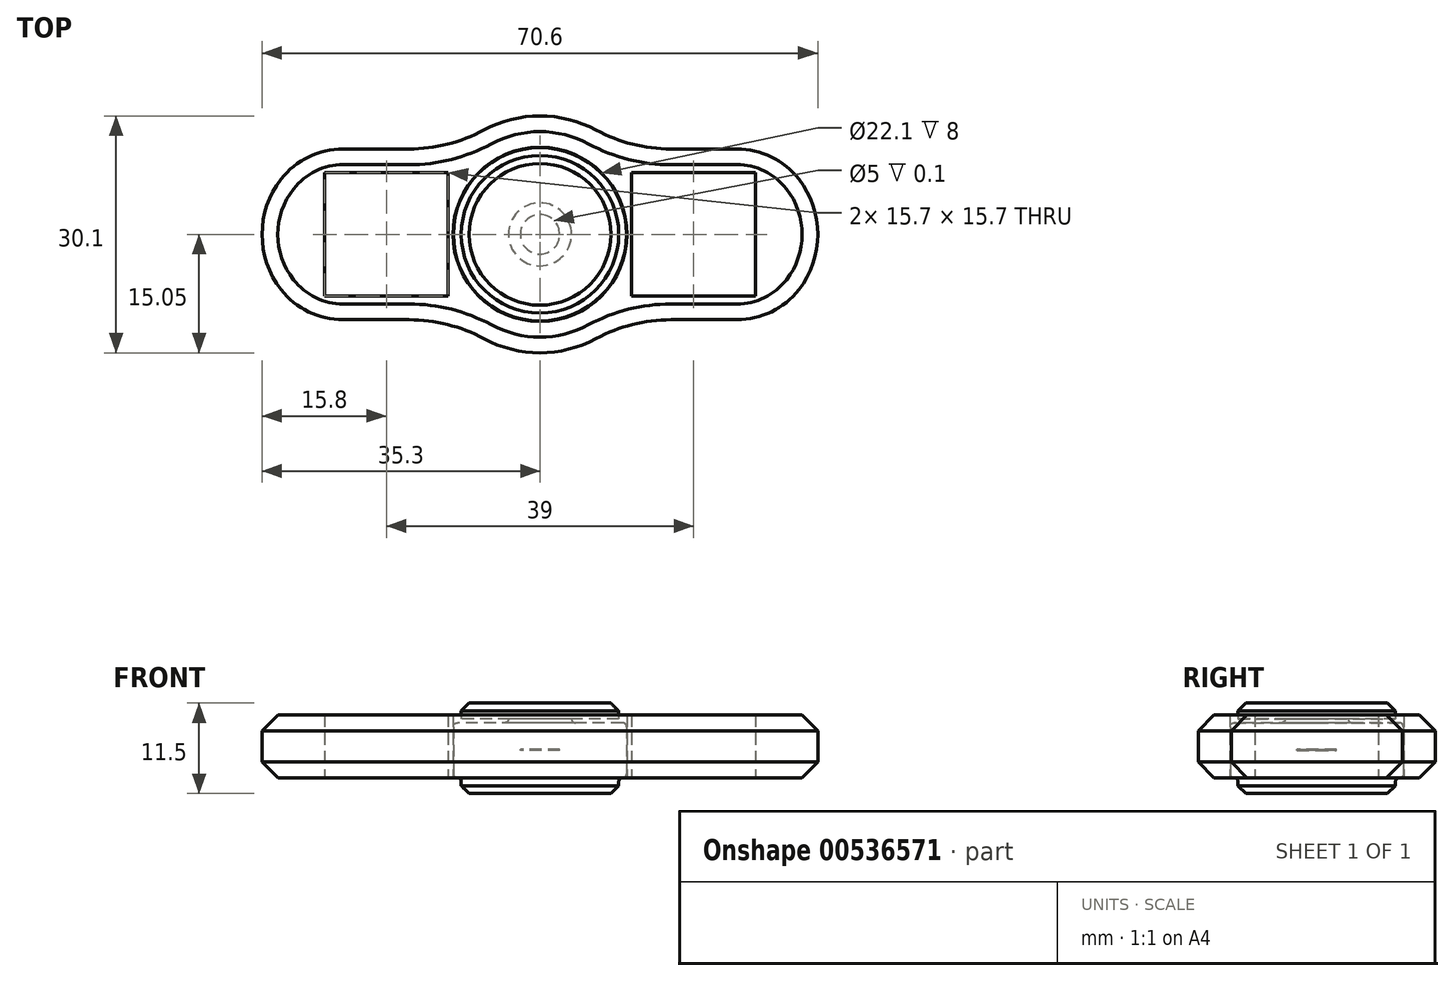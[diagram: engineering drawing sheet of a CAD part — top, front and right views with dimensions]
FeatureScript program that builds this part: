
annotation { "Feature Type Name" : "Feature", "Feature Type Description" : "" }
export const myFeature = defineFeature(function(context is Context, id is Id, definition is map)
    precondition{}
    {
        {
            var Q0;
            Q0=qCreatedBy(makeId("Top.planeOp"),FACE);
            var sketch = newSketch(context, id + "F0", { "sketchPlane" : qUnion([Q0])});
            skCircle(sketch, "E0", {"center": v(0, 0) * mm, "radius": 11 * mm});
            skCircle(sketch, "E1", {"center": v(0, 0) * mm, "radius": 4 * mm});
            skSolve(sketch);
        }
        {
            var Q0;
            Q0=makeQuery(id+"F0.imprint","IMPRINT",FACE,{"disambiguationData":[TD([[makeQuery(id+"F0.imprint","IMPRINT",EDGE,{"derivedFrom":sQuery(id+"F0.wireOp",EDGE,"E0")}),1.0]])]});
            extrude(context, id + "F1", {"entities" : qUnion([Q0]), "depth" : 7 * mm, "offsetDistance" : 25 * mm});
        }
        {
            var Q0;
            Q0=makeQuery(id+"F1.opExtrude","CAP_FACE",FACE,{"disambiguationData":[OSD([sQuery(id+"F0.wireOp",EDGE,"E0"),sQuery(id+"F0.wireOp",EDGE,"E1")])],"isStart":true});
            var sketch = newSketch(context, id + "F2", { "sketchPlane" : qUnion([Q0])});
            skCircle(sketch, "E2.0", {"center": v(0, 0) * mm, "radius": 11.05 * mm});
            skCircle(sketch, "E3.0", {"center": v(0, 0) * mm, "radius": 15.05 * mm});
            skLineSegment(sketch, "E4", {"start": v(0, 0) * mm, "end": v(-19.5, 0) * mm, "construction": true});
            skLineSegment(sketch, "E5.bottom", {"start": v(-27.35, -7.85) * mm, "end": v(-11.65, -7.85) * mm});
            skLineSegment(sketch, "E5.top", {"start": v(-27.35, 7.85) * mm, "end": v(-11.65, 7.85) * mm});
            skLineSegment(sketch, "E5.left", {"start": v(-27.35, -7.85) * mm, "end": v(-27.35, 7.85) * mm});
            skLineSegment(sketch, "E5.right", {"start": v(-11.65, -7.85) * mm, "end": v(-11.65, 7.85) * mm});
            skPoint(sketch, "E5.middle", {"position": v(-19.5, 0) * mm});
            skCircle(sketch, "E6", {"center": v(0, 0) * mm, "radius": 50 * mm, "construction": true});
            skLineSegment(sketch, "E7", {"start": v(-19.5, 0) * mm, "end": v(-35.3, 0) * mm, "construction": true});
            skLineSegment(sketch, "E8", {"start": v(-27.35, 7.85) * mm, "end": v(-27.35, 10.85) * mm, "construction": true});
            skLineSegment(sketch, "E9.0", {"start": v(-23, 10.85) * mm, "end": v(-27.35, 10.85) * mm});
            skLineSegment(sketch, "E9.1", {"start": v(0, 10.85) * mm, "end": v(-2.1, 10.85) * mm, "construction": true});
            skLineSegment(sketch, "E10.trimOffspring", {"start": v(-10.43, 10.85) * mm, "end": v(-23, 10.85) * mm});
            skLineSegment(sketch, "E11.MirrorCS", {"start": v(-10.43, -10.85) * mm, "end": v(-23, -10.85) * mm});
            skLineSegment(sketch, "E12.MirrorCS", {"start": v(-23, -10.85) * mm, "end": v(-27.35, -10.85) * mm});
            skArc(sketch, "E13", {"start": v(-27.35, 10.85) * mm, "mid": v(-35.3, 0) * mm, "end": v(-27.35, -10.85) * mm});
            skLineSegment(sketch, "E14.1.0", {"start": v(27.35, 7.85) * mm, "end": v(11.65, 7.85) * mm});
            skLineSegment(sketch, "E14.1.1", {"start": v(11.65, 7.85) * mm, "end": v(11.65, -7.85) * mm});
            skLineSegment(sketch, "E14.1.2", {"start": v(27.35, -7.85) * mm, "end": v(11.65, -7.85) * mm});
            skLineSegment(sketch, "E14.1.3", {"start": v(10.43, -10.85) * mm, "end": v(23, -10.85) * mm});
            skLineSegment(sketch, "E14.1.4", {"start": v(23, -10.85) * mm, "end": v(27.35, -10.85) * mm});
            skLineSegment(sketch, "E14.1.5", {"start": v(27.35, 7.85) * mm, "end": v(27.35, -7.85) * mm});
            skArc(sketch, "E14.1.6", {"start": v(27.35, -10.85) * mm, "mid": v(35.3, 0) * mm, "end": v(27.35, 10.85) * mm});
            skLineSegment(sketch, "E14.1.7", {"start": v(23, 10.85) * mm, "end": v(27.35, 10.85) * mm});
            skLineSegment(sketch, "E14.1.8", {"start": v(10.43, 10.85) * mm, "end": v(23, 10.85) * mm});
            skCircle(sketch, "E15", {"center": v(0, 0) * mm, "radius": 29.42 * mm, "construction": true});
            skSolve(sketch);
        }
        {
            var Q0;
            {var subQ5=sQuery(id+"F2.wireOp",EDGE,"E14.2.0");Q0=makeQuery(id+"F2.imprint","IMPRINT",FACE,{"disambiguationData":[TD([[makeQuery(id+"F2.imprint","IMPRINT",EDGE,{"derivedFrom":subQ5}),-1.0]])]});}
            var Q1;
            Q1=makeQuery(id+"F2.imprint","IMPRINT",FACE,{"disambiguationData":[TD([[makeQuery(id+"F2.imprint","IMPRINT",EDGE,{"derivedFrom":sQuery(id+"F2.wireOp",EDGE,"E2.0")}),-1.0]])]});
            var Q2;
            {var subQ6=sQuery(id+"F2.wireOp",EDGE,"E14.1.0");Q2=makeQuery(id+"F2.imprint","IMPRINT",FACE,{"disambiguationData":[TD([[makeQuery(id+"F2.imprint","IMPRINT",EDGE,{"derivedFrom":subQ6}),-1.0]])]});}
            var Q3;
            {var subQ5=sQuery(id+"F2.wireOp",EDGE,"E5.bottom");Q3=makeQuery(id+"F2.imprint","IMPRINT",FACE,{"disambiguationData":[TD([[makeQuery(id+"F2.imprint","IMPRINT",EDGE,{"derivedFrom":subQ5}),-1.0]])]});}
            extrude(context, id + "F3", {"entities" : qUnion([Q0, Q1, Q2, Q3]), "oppositeDirection" : true, "depth" : 8 * mm, "offsetDistance" : 25 * mm});
        }
        {
            var Q0;
            Q0=makeQuery(id+"F3.opExtrude","SWEPT_EDGE",EDGE,{"disambiguationData":[OSD([sQuery(id+"F2.wireOp",EDGE,"E3.0"),sQuery(id+"F2.wireOp",EDGE,"E14.2.3")])]});
            var Q1;
            Q1=makeQuery(id+"F3.opExtrude","SWEPT_EDGE",EDGE,{"disambiguationData":[OSD([sQuery(id+"F2.wireOp",EDGE,"E3.0"),sQuery(id+"F2.wireOp",EDGE,"E14.1.8")])]});
            var Q2;
            Q2=makeQuery(id+"F3.opExtrude","SWEPT_EDGE",EDGE,{"disambiguationData":[OSD([sQuery(id+"F2.wireOp",EDGE,"E3.0"),sQuery(id+"F2.wireOp",EDGE,"E14.2.8")])]});
            var Q3;
            Q3=makeQuery(id+"F3.opExtrude","SWEPT_EDGE",EDGE,{"disambiguationData":[OSD([sQuery(id+"F2.wireOp",EDGE,"E3.0"),sQuery(id+"F2.wireOp",EDGE,"E10.trimOffspring")])]});
            var Q4;
            Q4=makeQuery(id+"F3.opExtrude","SWEPT_EDGE",EDGE,{"disambiguationData":[OSD([sQuery(id+"F2.wireOp",EDGE,"E3.0"),sQuery(id+"F2.wireOp",EDGE,"E11.MirrorCS")])]});
            var Q5;
            Q5=makeQuery(id+"F3.opExtrude","SWEPT_EDGE",EDGE,{"disambiguationData":[OSD([sQuery(id+"F2.wireOp",EDGE,"E3.0"),sQuery(id+"F2.wireOp",EDGE,"E14.1.3")])]});
            fillet(context, id + "F4", {"entities" : qUnion([Q0, Q1, Q2, Q3, Q4, Q5]), "radius" : 20 * mm, "tangentPropagation" : true, "allowEdgeOverflow" : false});
        }
        {
            var Q0;
            Q0=makeQuery(id+"F3.opExtrude","SWEPT_EDGE",EDGE,{"disambiguationData":[OSD([sQuery(id+"F2.wireOp",EDGE,"E14.2.4"),sQuery(id+"F2.wireOp",EDGE,"E14.2.6")])]});
            var Q1;
            Q1=makeQuery(id+"F3.opExtrude","SWEPT_EDGE",EDGE,{"disambiguationData":[OSD([sQuery(id+"F2.wireOp",EDGE,"E14.2.6"),sQuery(id+"F2.wireOp",EDGE,"E14.2.7")])]});
            var Q2;
            Q2=makeQuery(id+"F3.opExtrude","SWEPT_EDGE",EDGE,{"disambiguationData":[OSD([sQuery(id+"F2.wireOp",EDGE,"E9.0"),sQuery(id+"F2.wireOp",EDGE,"E13")])]});
            var Q3;
            Q3=makeQuery(id+"F3.opExtrude","SWEPT_EDGE",EDGE,{"disambiguationData":[OSD([sQuery(id+"F2.wireOp",EDGE,"E12.MirrorCS"),sQuery(id+"F2.wireOp",EDGE,"E13")])]});
            var Q4;
            Q4=makeQuery(id+"F3.opExtrude","SWEPT_EDGE",EDGE,{"disambiguationData":[OSD([sQuery(id+"F2.wireOp",EDGE,"E14.1.4"),sQuery(id+"F2.wireOp",EDGE,"E14.1.6")])]});
            var Q5;
            Q5=makeQuery(id+"F3.opExtrude","SWEPT_EDGE",EDGE,{"disambiguationData":[OSD([sQuery(id+"F2.wireOp",EDGE,"E14.1.6"),sQuery(id+"F2.wireOp",EDGE,"E14.1.7")])]});
            fillet(context, id + "F5", {"entities" : qUnion([Q0, Q1, Q2, Q3, Q4, Q5]), "radius" : 10 * mm, "tangentPropagation" : true, "allowEdgeOverflow" : false});
        }
        {
            var Q0;
            Q0=makeQuery(id+"F3.opExtrude","CAP_EDGE",EDGE,{"disambiguationData":[OSD([sQuery(id+"F2.wireOp",EDGE,"E14.2.6")])],"isStart":false});
            var Q1;
            Q1=makeQuery(id+"F3.opExtrude","CAP_EDGE",EDGE,{"disambiguationData":[OSD([sQuery(id+"F2.wireOp",EDGE,"E14.1.6")])],"isStart":false});
            var Q2;
            {var subQ0=sQuery(id+"F2.wireOp",EDGE,"E13");var subQ1=sQuery(id+"F2.wireOp",EDGE,"E9.0");Q2=makeQuery(id+"F5.opFillet","BLEND_EDGE",EDGE,{"blendedFrom":[makeQuery(id+"F3.opExtrude","SWEPT_EDGE",EDGE,{"disambiguationData":[OSD([subQ1,subQ0])]}),makeQuery(id+"F3.opExtrude","CAP_FACE",FACE,{"disambiguationData":[OSD([sQuery(id+"F2.wireOp",EDGE,"E2.0"),sQuery(id+"F2.wireOp",EDGE,"E3.0"),sQuery(id+"F2.wireOp",EDGE,"E5.bottom"),sQuery(id+"F2.wireOp",EDGE,"E5.top"),sQuery(id+"F2.wireOp",EDGE,"E5.left"),sQuery(id+"F2.wireOp",EDGE,"E5.right"),subQ1,sQuery(id+"F2.wireOp",EDGE,"E10.trimOffspring"),sQuery(id+"F2.wireOp",EDGE,"E11.MirrorCS"),sQuery(id+"F2.wireOp",EDGE,"E12.MirrorCS"),subQ0,sQuery(id+"F2.wireOp",EDGE,"E14.1.0"),sQuery(id+"F2.wireOp",EDGE,"E14.1.1"),sQuery(id+"F2.wireOp",EDGE,"E14.1.2"),sQuery(id+"F2.wireOp",EDGE,"E14.1.3"),sQuery(id+"F2.wireOp",EDGE,"E14.1.4"),sQuery(id+"F2.wireOp",EDGE,"E14.1.5"),sQuery(id+"F2.wireOp",EDGE,"E14.1.6"),sQuery(id+"F2.wireOp",EDGE,"E14.1.7"),sQuery(id+"F2.wireOp",EDGE,"E14.1.8"),sQuery(id+"F2.wireOp",EDGE,"E14.2.0"),sQuery(id+"F2.wireOp",EDGE,"E14.2.1"),sQuery(id+"F2.wireOp",EDGE,"E14.2.2"),sQuery(id+"F2.wireOp",EDGE,"E14.2.3"),sQuery(id+"F2.wireOp",EDGE,"E14.2.4"),sQuery(id+"F2.wireOp",EDGE,"E14.2.5"),sQuery(id+"F2.wireOp",EDGE,"E14.2.6"),sQuery(id+"F2.wireOp",EDGE,"E14.2.7"),sQuery(id+"F2.wireOp",EDGE,"E14.2.8")])],"isStart":false})],"blendedInto":[makeQuery(id+"F3.opExtrude","CAP_FACE",FACE,{"disambiguationData":[OSD([sQuery(id+"F2.wireOp",EDGE,"E2.0"),sQuery(id+"F2.wireOp",EDGE,"E3.0"),sQuery(id+"F2.wireOp",EDGE,"E5.bottom"),sQuery(id+"F2.wireOp",EDGE,"E5.top"),sQuery(id+"F2.wireOp",EDGE,"E5.left"),sQuery(id+"F2.wireOp",EDGE,"E5.right"),subQ1,sQuery(id+"F2.wireOp",EDGE,"E10.trimOffspring"),sQuery(id+"F2.wireOp",EDGE,"E11.MirrorCS"),sQuery(id+"F2.wireOp",EDGE,"E12.MirrorCS"),subQ0,sQuery(id+"F2.wireOp",EDGE,"E14.1.0"),sQuery(id+"F2.wireOp",EDGE,"E14.1.1"),sQuery(id+"F2.wireOp",EDGE,"E14.1.2"),sQuery(id+"F2.wireOp",EDGE,"E14.1.3"),sQuery(id+"F2.wireOp",EDGE,"E14.1.4"),sQuery(id+"F2.wireOp",EDGE,"E14.1.5"),sQuery(id+"F2.wireOp",EDGE,"E14.1.6"),sQuery(id+"F2.wireOp",EDGE,"E14.1.7"),sQuery(id+"F2.wireOp",EDGE,"E14.1.8"),sQuery(id+"F2.wireOp",EDGE,"E14.2.0"),sQuery(id+"F2.wireOp",EDGE,"E14.2.1"),sQuery(id+"F2.wireOp",EDGE,"E14.2.2"),sQuery(id+"F2.wireOp",EDGE,"E14.2.3"),sQuery(id+"F2.wireOp",EDGE,"E14.2.4"),sQuery(id+"F2.wireOp",EDGE,"E14.2.5"),sQuery(id+"F2.wireOp",EDGE,"E14.2.6"),sQuery(id+"F2.wireOp",EDGE,"E14.2.7"),sQuery(id+"F2.wireOp",EDGE,"E14.2.8")])],"isStart":false})]});}
            var Q3;
            Q3=makeQuery(id+"F3.opExtrude","CAP_EDGE",EDGE,{"disambiguationData":[OSD([sQuery(id+"F2.wireOp",EDGE,"E14.2.6")])],"isStart":true});
            var Q4;
            Q4=makeQuery(id+"F3.opExtrude","CAP_EDGE",EDGE,{"disambiguationData":[OSD([sQuery(id+"F2.wireOp",EDGE,"E13")])],"isStart":true});
            var Q5;
            Q5=makeQuery(id+"F3.opExtrude","CAP_EDGE",EDGE,{"disambiguationData":[OSD([sQuery(id+"F2.wireOp",EDGE,"E14.1.6")])],"isStart":true});
            chamfer(context, id + "F6", {"entities" : qUnion([Q0, Q1, Q2, Q3, Q4, Q5]), "width" : 2 * mm, "tangentPropagation" : true});
        }
        {
            var Q0;
            Q0=makeQuery(id+"F3.opExtrude","CAP_FACE",FACE,{"disambiguationData":[OSD([sQuery(id+"F2.wireOp",EDGE,"E2.0"),sQuery(id+"F2.wireOp",EDGE,"E3.0"),sQuery(id+"F2.wireOp",EDGE,"E5.bottom"),sQuery(id+"F2.wireOp",EDGE,"E5.top"),sQuery(id+"F2.wireOp",EDGE,"E5.left"),sQuery(id+"F2.wireOp",EDGE,"E5.right"),sQuery(id+"F2.wireOp",EDGE,"E9.0"),sQuery(id+"F2.wireOp",EDGE,"E10.trimOffspring"),sQuery(id+"F2.wireOp",EDGE,"E11.MirrorCS"),sQuery(id+"F2.wireOp",EDGE,"E12.MirrorCS"),sQuery(id+"F2.wireOp",EDGE,"E13"),sQuery(id+"F2.wireOp",EDGE,"E14.1.0"),sQuery(id+"F2.wireOp",EDGE,"E14.1.1"),sQuery(id+"F2.wireOp",EDGE,"E14.1.2"),sQuery(id+"F2.wireOp",EDGE,"E14.1.3"),sQuery(id+"F2.wireOp",EDGE,"E14.1.4"),sQuery(id+"F2.wireOp",EDGE,"E14.1.5"),sQuery(id+"F2.wireOp",EDGE,"E14.1.6"),sQuery(id+"F2.wireOp",EDGE,"E14.1.7"),sQuery(id+"F2.wireOp",EDGE,"E14.1.8"),sQuery(id+"F2.wireOp",EDGE,"E14.2.0"),sQuery(id+"F2.wireOp",EDGE,"E14.2.1"),sQuery(id+"F2.wireOp",EDGE,"E14.2.2"),sQuery(id+"F2.wireOp",EDGE,"E14.2.3"),sQuery(id+"F2.wireOp",EDGE,"E14.2.4"),sQuery(id+"F2.wireOp",EDGE,"E14.2.5"),sQuery(id+"F2.wireOp",EDGE,"E14.2.6"),sQuery(id+"F2.wireOp",EDGE,"E14.2.7"),sQuery(id+"F2.wireOp",EDGE,"E14.2.8")])],"isStart":true});
            var sketch = newSketch(context, id + "F7", { "sketchPlane" : qUnion([Q0])});
            skLineSegment(sketch, "E16.0", {"start": v(29.35, 5.87) * mm, "end": v(29.35, -5.87) * mm});
            skArc(sketch, "E17.0", {"start": v(31.3, 5.78) * mm, "mid": v(32.9, -0.47) * mm, "end": v(29.35, -5.87) * mm});
            skArc(sketch, "E17.1", {"start": v(31.3, -5.78) * mm, "mid": v(33.3, 0) * mm, "end": v(31.3, 5.78) * mm});
            skArc(sketch, "E17.2", {"start": v(29.35, 5.87) * mm, "mid": v(32.9, 0.47) * mm, "end": v(31.3, -5.78) * mm});
            skArc(sketch, "E18.0", {"start": v(12.39, 33.05) * mm, "mid": v(11.1, 32.77) * mm, "end": v(9.89, 32.28) * mm});
            skArc(sketch, "E18.1", {"start": v(22.43, 27.25) * mm, "mid": v(18.4, 31.87) * mm, "end": v(12.39, 33.05) * mm});
            skArc(sketch, "E18.2", {"start": v(23.01, 24.7) * mm, "mid": v(22.83, 26) * mm, "end": v(22.43, 27.25) * mm});
            skLineSegment(sketch, "E19.0", {"start": v(9.89, 32.28) * mm, "end": v(23.01, 24.7) * mm});
            skArc(sketch, "E20.0", {"start": v(-31.3, -5.78) * mm, "mid": v(-30.4, -6.76) * mm, "end": v(-29.35, -7.57) * mm});
            skArc(sketch, "E20.1", {"start": v(-31.3, 5.78) * mm, "mid": v(-33.3, 0) * mm, "end": v(-31.3, -5.78) * mm});
            skArc(sketch, "E20.2", {"start": v(-29.35, 7.57) * mm, "mid": v(-30.4, 6.76) * mm, "end": v(-31.3, 5.78) * mm});
            skLineSegment(sketch, "E21.0", {"start": v(-29.35, -7.57) * mm, "end": v(-29.35, 7.57) * mm});
            skSolve(sketch);
        }
        {
            var Q0;
            Q0=makeQuery(id+"F1.opExtrude","CAP_FACE",FACE,{"disambiguationData":[OSD([sQuery(id+"F0.wireOp",EDGE,"E0"),sQuery(id+"F0.wireOp",EDGE,"E1")])],"isStart":true});
            var sketch = newSketch(context, id + "F8", { "sketchPlane" : qUnion([Q0])});
            skCircle(sketch, "E22.0", {"center": v(0, 0) * mm, "radius": 10 * mm});
            skSolve(sketch);
        }
        {
            var Q0;
            Q0=makeQuery(id+"F8.imprint","IMPRINT",FACE,{"disambiguationData":[TD([[makeQuery(id+"F8.imprint","IMPRINT",EDGE,{"derivedFrom":sQuery(id+"F8.wireOp",EDGE,"E22.0")}),1.0]])]});
            var Q1;
            Q1=makeQuery(id+"F8.imprint","IMPRINT",FACE,{"disambiguationData":[TD([[makeQuery(id+"F8.imprint","IMPRINT",EDGE,{"derivedFrom":sQuery(id+"F8.wireOp",EDGE,"c407c948-2510-426a-b12c-06ac0bc9cf64.0")}),-1.0]])]});
            var Q2;
            Q2=makeQuery(id+"F8.imprint","IMPRINT",FACE,{"disambiguationData":[TD([[makeQuery(id+"F8.imprint","IMPRINT",EDGE,{"derivedFrom":sQuery(id+"F8.wireOp",EDGE,"c407c948-2510-426a-b12c-06ac0bc9cf64.0")}),1.0]])]});
            var Q3;
            Q3=makeQuery(id+"F8.imprint","IMPRINT",FACE,{"disambiguationData":[TD([[makeQuery(id+"F8.imprint","IMPRINT",EDGE,{"derivedFrom":makeQuery(id+"F1.opExtrude","CAP_EDGE",EDGE,{"disambiguationData":[OSD([sQuery(id+"F0.wireOp",EDGE,"E1")])],"isStart":true})}),-1.0]])]});
            extrude(context, id + "F9", {"entities" : qUnion([Q0, Q1, Q2, Q3]), "depth" : 2 * mm, "offsetDistance" : 25 * mm});
        }
        {
            var Q0;
            Q0=makeQuery(id+"F8.imprint","IMPRINT",FACE,{"disambiguationData":[TD([[makeQuery(id+"F8.imprint","IMPRINT",EDGE,{"derivedFrom":makeQuery(id+"F1.opExtrude","CAP_EDGE",EDGE,{"disambiguationData":[OSD([sQuery(id+"F0.wireOp",EDGE,"E1")])],"isStart":true})}),-1.0]])]});
            extrude(context, id + "F10", {"entities" : qUnion([Q0]), "operationType" : NewBodyOperationType.ADD, "oppositeDirection" : true, "depth" : 7.5 * mm, "offsetDistance" : 25 * mm});
        }
        {
            var Q0;
            Q0=makeQuery(id+"F10.opExtrude","CAP_FACE",FACE,{"disambiguationData":[OSD([sQuery(id+"F0.wireOp",EDGE,"E1")])],"isStart":false});
            var sketch = newSketch(context, id + "F11", { "sketchPlane" : qUnion([Q0])});
            skCircle(sketch, "E23.0", {"center": v(0, 0) * mm, "radius": 10 * mm});
            skCircle(sketch, "E24.0", {"center": v(0, 0) * mm, "radius": 2.5 * mm});
            skSolve(sketch);
        }
        {
            var Q0;
            Q0=makeQuery(id+"F11.imprint","IMPRINT",FACE,{"disambiguationData":[TD([[makeQuery(id+"F11.imprint","IMPRINT",EDGE,{"derivedFrom":sQuery(id+"F11.wireOp",EDGE,"E24.0")}),1.0]])]});
            extrude(context, id + "F12", {"entities" : qUnion([Q0]), "operationType" : NewBodyOperationType.REMOVE, "oppositeDirection" : true, "depth" : 4 * mm, "offsetDistance" : 25 * mm});
        }
        {
            var Q0;
            Q0=makeQuery(id+"F11.imprint","IMPRINT",FACE,{"disambiguationData":[TD([[makeQuery(id+"F11.imprint","IMPRINT",EDGE,{"derivedFrom":sQuery(id+"F11.wireOp",EDGE,"E23.0")}),1.0]])]});
            var Q1;
            Q1=makeQuery(id+"F11.imprint","IMPRINT",FACE,{"disambiguationData":[TD([[makeQuery(id+"F11.imprint","IMPRINT",EDGE,{"derivedFrom":sQuery(id+"F11.wireOp",EDGE,"a1f51509-8c7b-4646-a507-0ed3af852b90.0")}),-1.0]])]});
            var Q2;
            Q2=makeQuery(id+"F11.imprint","IMPRINT",FACE,{"disambiguationData":[TD([[makeQuery(id+"F11.imprint","IMPRINT",EDGE,{"derivedFrom":sQuery(id+"F11.wireOp",EDGE,"15deca98-b56f-4649-b585-fda4b9412a6e.0")}),1.0]])]});
            var Q3;
            Q3=makeQuery(id+"F11.imprint","IMPRINT",FACE,{"disambiguationData":[TD([[makeQuery(id+"F11.imprint","IMPRINT",EDGE,{"derivedFrom":sQuery(id+"F11.wireOp",EDGE,"a1f51509-8c7b-4646-a507-0ed3af852b90.0")}),1.0]])]});
            var Q4;
            Q4=makeQuery(id+"F11.imprint","IMPRINT",FACE,{"disambiguationData":[TD([[makeQuery(id+"F11.imprint","IMPRINT",EDGE,{"derivedFrom":sQuery(id+"F11.wireOp",EDGE,"E24.0")}),-1.0]])]});
            var Q5;
            Q5=makeQuery(id+"F11.imprint","IMPRINT",FACE,{"disambiguationData":[TD([[makeQuery(id+"F11.imprint","IMPRINT",EDGE,{"derivedFrom":sQuery(id+"F11.wireOp",EDGE,"E24.0")}),1.0]])]});
            extrude(context, id + "F13", {"entities" : qUnion([Q0, Q1, Q2, Q3, Q4, Q5]), "depth" : 2 * mm, "offsetDistance" : 25 * mm});
        }
        {
            var Q0;
            Q0=makeQuery(id+"F11.imprint","IMPRINT",FACE,{"disambiguationData":[TD([[makeQuery(id+"F11.imprint","IMPRINT",EDGE,{"derivedFrom":sQuery(id+"F11.wireOp",EDGE,"E24.0")}),1.0]])]});
            extrude(context, id + "F14", {"entities" : qUnion([Q0]), "operationType" : NewBodyOperationType.ADD, "oppositeDirection" : true, "depth" : 3.9 * mm, "offsetDistance" : 25 * mm});
        }
        {
            var Q0;
            Q0=makeQuery(id+"F9.opExtrude","CAP_FACE",FACE,{"disambiguationData":[OSD([sQuery(id+"F8.wireOp",EDGE,"E22.0")])],"isStart":false});
            var Q1;
            Q1=makeQuery(id+"F13.opExtrude","CAP_EDGE",EDGE,{"disambiguationData":[OSD([sQuery(id+"F11.wireOp",EDGE,"E23.0")])],"isStart":false});
            chamfer(context, id + "F15", {"entities" : qUnion([Q0, Q1]), "width" : 1 * mm, "tangentPropagation" : true});
        }
        {
            var Q0;
            Q0=makeQuery(id+"F1.opExtrude","CAP_FACE",FACE,{"disambiguationData":[OSD([sQuery(id+"F0.wireOp",EDGE,"E0"),sQuery(id+"F0.wireOp",EDGE,"E1")])],"isStart":true});
            var Q1;
            Q1=makeQuery(id+"F1.opExtrude","CAP_FACE",FACE,{"disambiguationData":[OSD([sQuery(id+"F0.wireOp",EDGE,"E0"),sQuery(id+"F0.wireOp",EDGE,"E1")])],"isStart":false});
            fillet(context, id + "F16", {"entities" : qUnion([Q0, Q1]), "radius" : .5 * mm, "tangentPropagation" : true, "allowEdgeOverflow" : false});
        }
    });
